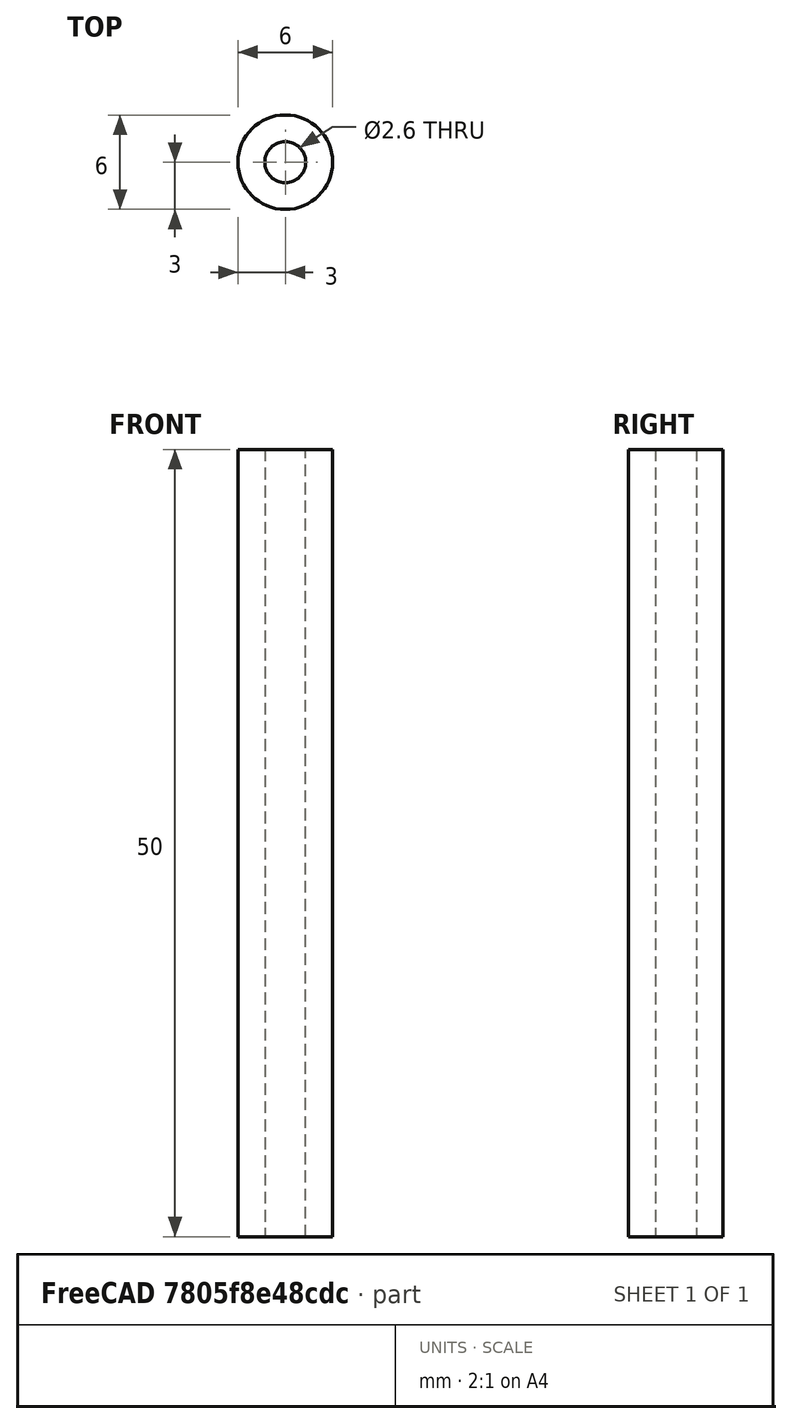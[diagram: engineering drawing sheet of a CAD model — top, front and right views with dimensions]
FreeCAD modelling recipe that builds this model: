
FCSTD DOCUMENT  (FreeCAD 0.19R24291 (Git))
Label: windShaftv2
License: All rights reserved
LicenseURL: http://en.wikipedia.org/wiki/All_rights_reserved
objects: Sketcher::SketchObject×1, PartDesign::Pad×1, PartDesign::Body×1
note: 4 computed .brp shape members not serialized (recipe doc carries the construction recipe); baked Part::Feature solids carry a one-line shape summary decoded from their .brp

FEATURE [Sketcher::SketchObject] Sketch
  FullyConstrained = true
  MapMode = 5
  Support = -> [XY_Plane]
  sketch-geometry (2):
    g0: Circle CenterX=0 CenterY=0 CenterZ=0 NormalX=0 NormalY=0 NormalZ=1 AngleXU=0 Radius=3
    g1: Circle CenterX=0 CenterY=0 CenterZ=0 NormalX=0 NormalY=0 NormalZ=1 AngleXU=0 Radius=1.3
  constraints (4):
    c: Coincident(g0,g-1)
    c: Coincident(g1,g0)
    c: Radius(g0) = 3
    c: Radius(g1) = 1.3
FEATURE [PartDesign::Pad] Pad
  Direction = (1,1,1)
  Length = 50
  Length2 = 100
  Profile = -> Sketch
  Type = 0
FEATURE [PartDesign::Body] Body
  Group = -> [Sketch,Pad]
  Origin = -> Origin
  Tip = -> Pad
